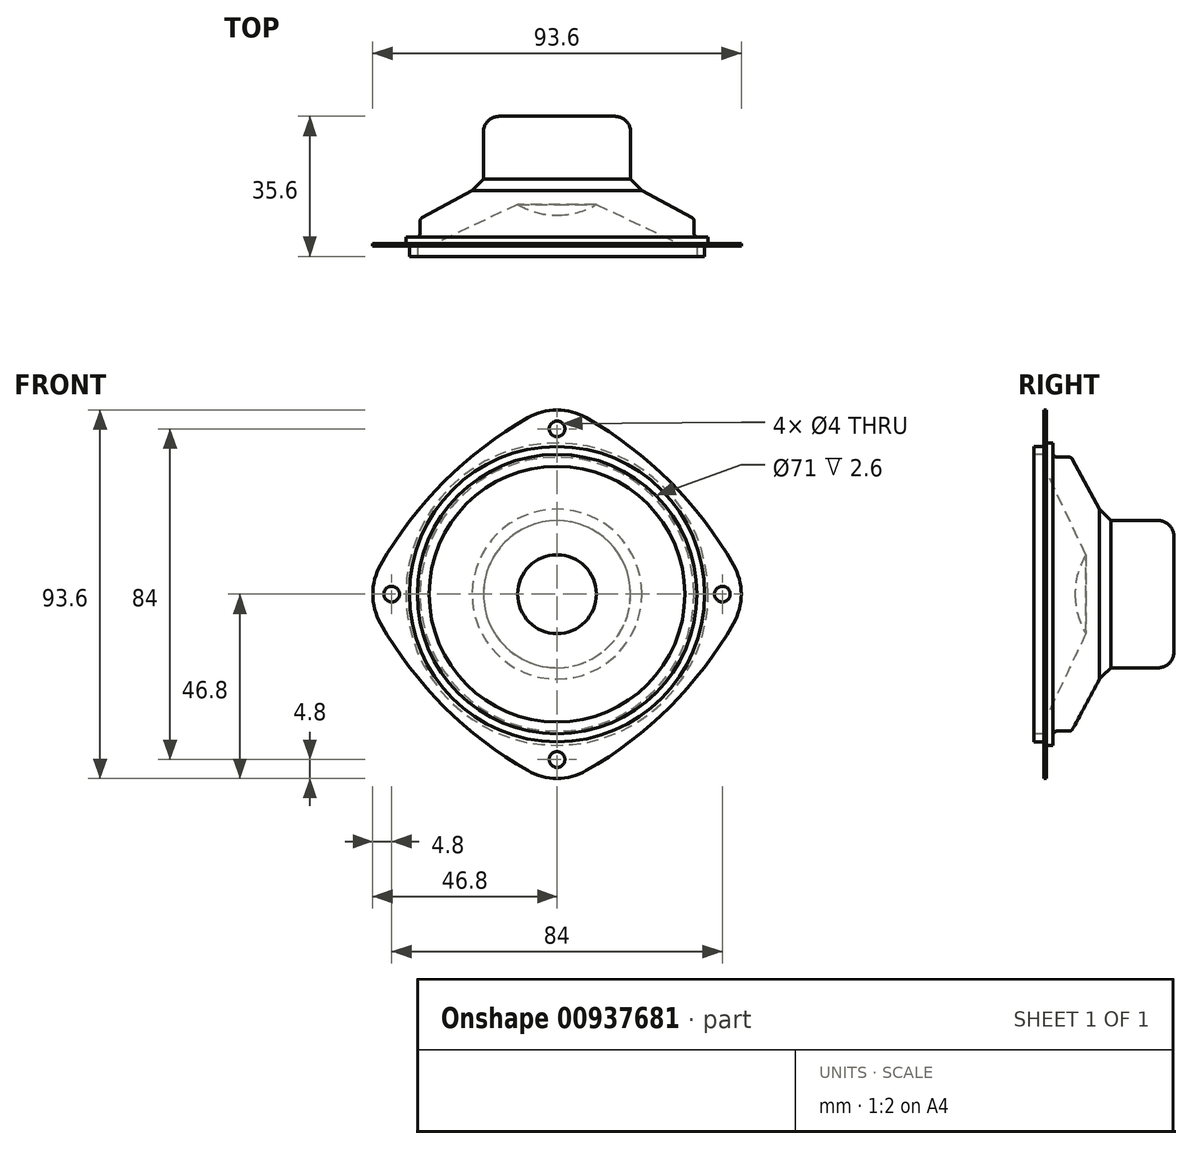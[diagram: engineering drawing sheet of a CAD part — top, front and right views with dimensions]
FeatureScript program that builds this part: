
annotation { "Feature Type Name" : "Feature", "Feature Type Description" : "" }
export const myFeature = defineFeature(function(context is Context, id is Id, definition is map)
    precondition{}
    {
        {
            var Q0;
            Q0=qCreatedBy(makeId("Top.planeOp"),FACE);
            var sketch = newSketch(context, id + "F0", { "sketchPlane" : qUnion([Q0])});
            skLineSegment(sketch, "E0", {"start": v(0, -15.16) * mm, "end": v(0, 70.73) * mm, "construction": true});
            skLineSegment(sketch, "E1", {"start": v(37.5, 0) * mm, "end": v(46.8, 0) * mm});
            skLineSegment(sketch, "E2", {"start": v(37.5, 0) * mm, "end": v(37.5, -2.6) * mm});
            skLineSegment(sketch, "E3", {"start": v(37.5, -2.6) * mm, "end": v(35.5, -2.6) * mm});
            skLineSegment(sketch, "E4", {"start": v(35.5, -2.6) * mm, "end": v(35.5, 0) * mm});
            skLineSegment(sketch, "E5", {"start": v(46.8, 0) * mm, "end": v(46.8, 0.65) * mm});
            skLineSegment(sketch, "E6", {"start": v(46.8, 0.65) * mm, "end": v(38.4, 0.65) * mm});
            skLineSegment(sketch, "E7", {"start": v(38.4, 0.65) * mm, "end": v(38.4, 2.3) * mm});
            skLineSegment(sketch, "E8", {"start": v(38.4, 2.3) * mm, "end": v(34.8, 2.3) * mm});
            skLineSegment(sketch, "E9", {"start": v(34.8, 2.3) * mm, "end": v(34.8, 7) * mm});
            skLineSegment(sketch, "E10", {"start": v(34.8, 7) * mm, "end": v(21.58, 14.1) * mm});
            skLineSegment(sketch, "E11", {"start": v(21.58, 14.1) * mm, "end": v(18.7, 17) * mm});
            skLineSegment(sketch, "E12", {"start": v(18.7, 17) * mm, "end": v(18.7, 33) * mm});
            skLineSegment(sketch, "E13", {"start": v(18.7, 33) * mm, "end": v(0, 33) * mm});
            skLineSegment(sketch, "E14", {"start": v(0, 0) * mm, "end": v(35.5, 0) * mm});
            skLineSegment(sketch, "E15", {"start": v(0, 33) * mm, "end": v(0, 0) * mm});
            skLineSegment(sketch, "E16", {"start": v(32.48, 0) * mm, "end": v(10.02, 10.63) * mm});
            skArc(sketch, "E17", {"start": v(10.02, 10.63) * mm, "mid": v(5.2, 8.58) * mm, "end": v(0, 7.89) * mm});
            skSolve(sketch);
        }
        {
            var Q0;
            Q0=makeQuery(id+"F0.imprint","IMPRINT",FACE,{"disambiguationData":[TD([[makeQuery(id+"F0.imprint","IMPRINT",EDGE,{"derivedFrom":sQuery(id+"F0.wireOp",EDGE,"E1")}),1.0]])]});
            var Q1;
            Q1=sQuery(id+"F0.wireOp",EDGE,"E0");
            revolve(context, id + "F1", {"surfaceOperationType" : NewSurfaceOperationType.NEW, "entities" : qUnion([Q0]), "axis" : qUnion([Q1]), "revolveType" : RevolveType.FULL});
        }
        {
            var Q0;
            Q0=makeQuery(id+"F1.opRevolve","SWEPT_EDGE",EDGE,{"disambiguationData":[OSD([sQuery(id+"F0.wireOp",EDGE,"E12"),sQuery(id+"F0.wireOp",EDGE,"E13")])]});
            fillet(context, id + "F2", {"entities" : qUnion([Q0]), "radius" : 4 * mm, "tangentPropagation" : true, "allowEdgeOverflow" : false});
        }
        {
            var Q0;
            Q0=makeQuery(id+"F1.opRevolve","SWEPT_EDGE",EDGE,{"disambiguationData":[OSD([sQuery(id+"F0.wireOp",EDGE,"E9"),sQuery(id+"F0.wireOp",EDGE,"E10")])]});
            var Q1;
            Q1=makeQuery(id+"F1.opRevolve","SWEPT_EDGE",EDGE,{"disambiguationData":[OSD([sQuery(id+"F0.wireOp",EDGE,"E8"),sQuery(id+"F0.wireOp",EDGE,"E9")])]});
            fillet(context, id + "F3", {"entities" : qUnion([Q0, Q1]), "radius" : 1 * mm, "tangentPropagation" : true, "allowEdgeOverflow" : false});
        }
        {
            var Q0;
            Q0=makeQuery(id+"F1.opRevolve","SWEPT_FACE",FACE,{"disambiguationData":[OSD([sQuery(id+"F0.wireOp",EDGE,"E1")])]});
            var sketch = newSketch(context, id + "F4", { "sketchPlane" : qUnion([Q0])});
            skCircle(sketch, "E18", {"center": v(0, 42) * mm, "radius": 2 * mm});
            skCircle(sketch, "E19.1.0", {"center": v(-42, 0) * mm, "radius": 2 * mm});
            skCircle(sketch, "E19.2.0", {"center": v(0, -42) * mm, "radius": 2 * mm});
            skCircle(sketch, "E19.3.0", {"center": v(42, 0) * mm, "radius": 2 * mm});
            skPoint(sketch, "E19.center", {"position": v(0, 0) * mm});
            skArc(sketch, "E20", {"start": v(7.42, 44.83) * mm, "mid": v(0, 46.8) * mm, "end": v(-7.42, 44.83) * mm});
            skArc(sketch, "E21.1.0", {"start": v(-44.83, 7.42) * mm, "mid": v(-46.8, 0) * mm, "end": v(-44.83, -7.42) * mm});
            skArc(sketch, "E21.2.0", {"start": v(-7.42, -44.83) * mm, "mid": v(0, -46.8) * mm, "end": v(7.42, -44.83) * mm});
            skArc(sketch, "E21.3.0", {"start": v(44.83, -7.42) * mm, "mid": v(46.8, 0) * mm, "end": v(44.83, 7.42) * mm});
            skArc(sketch, "E22", {"start": v(44.83, 7.42) * mm, "mid": v(28.65, 28.65) * mm, "end": v(7.42, 44.83) * mm});
            skArc(sketch, "E23.1.0", {"start": v(7.42, -44.83) * mm, "mid": v(28.65, -28.65) * mm, "end": v(44.83, -7.42) * mm});
            skArc(sketch, "E23.2.0", {"start": v(-44.83, -7.42) * mm, "mid": v(-28.65, -28.65) * mm, "end": v(-7.42, -44.83) * mm});
            skArc(sketch, "E23.3.0", {"start": v(-7.42, 44.83) * mm, "mid": v(-28.65, 28.65) * mm, "end": v(-44.83, 7.42) * mm});
            skLineSegment(sketch, "E23.anchor1", {"start": v(0, 0) * mm, "end": v(-42.06, -42.06) * mm, "construction": true});
            skLineSegment(sketch, "E23.anchor2", {"start": v(0, 0) * mm, "end": v(42.06, -42.06) * mm, "construction": true});
            skCircle(sketch, "E24", {"center": v(0, 0) * mm, "radius": 46.8 * mm});
            skSolve(sketch);
        }
        {
            var Q0;
            {var subQ0=sQuery(id+"F4.wireOp",EDGE,"E23.1.0");Q0=makeQuery(id+"F4.imprint","IMPRINT",FACE,{"disambiguationData":[TD([[makeQuery(id+"F4.imprint","IMPRINT",EDGE,{"derivedFrom":subQ0}),-1.0]])]});}
            var Q1;
            {var subQ0=sQuery(id+"F4.wireOp",EDGE,"E23.2.0");Q1=makeQuery(id+"F4.imprint","IMPRINT",FACE,{"disambiguationData":[TD([[makeQuery(id+"F4.imprint","IMPRINT",EDGE,{"derivedFrom":subQ0}),-1.0]])]});}
            var Q2;
            {var subQ0=sQuery(id+"F4.wireOp",EDGE,"E23.3.0");Q2=makeQuery(id+"F4.imprint","IMPRINT",FACE,{"disambiguationData":[TD([[makeQuery(id+"F4.imprint","IMPRINT",EDGE,{"derivedFrom":subQ0}),-1.0]])]});}
            var Q3;
            {var subQ0=sQuery(id+"F4.wireOp",EDGE,"E22");Q3=makeQuery(id+"F4.imprint","IMPRINT",FACE,{"disambiguationData":[TD([[makeQuery(id+"F4.imprint","IMPRINT",EDGE,{"derivedFrom":subQ0}),-1.0]])]});}
            var Q4;
            Q4=makeQuery(id+"F4.imprint","IMPRINT",FACE,{"disambiguationData":[TD([[makeQuery(id+"F4.imprint","IMPRINT",EDGE,{"derivedFrom":sQuery(id+"F4.wireOp",EDGE,"E19.2.0")}),1.0]])]});
            var Q5;
            Q5=makeQuery(id+"F4.imprint","IMPRINT",FACE,{"disambiguationData":[TD([[makeQuery(id+"F4.imprint","IMPRINT",EDGE,{"derivedFrom":sQuery(id+"F4.wireOp",EDGE,"E18")}),1.0]])]});
            var Q6;
            Q6=makeQuery(id+"F4.imprint","IMPRINT",FACE,{"disambiguationData":[TD([[makeQuery(id+"F4.imprint","IMPRINT",EDGE,{"derivedFrom":sQuery(id+"F4.wireOp",EDGE,"E19.1.0")}),1.0]])]});
            var Q7;
            Q7=makeQuery(id+"F4.imprint","IMPRINT",FACE,{"disambiguationData":[TD([[makeQuery(id+"F4.imprint","IMPRINT",EDGE,{"derivedFrom":sQuery(id+"F4.wireOp",EDGE,"E19.3.0")}),1.0]])]});
            extrude(context, id + "F5", {"entities" : qUnion([Q0, Q1, Q2, Q3, Q4, Q5, Q6, Q7]), "operationType" : NewBodyOperationType.REMOVE, "oppositeDirection" : true, "depth" : 25 * mm, "offsetDistance" : 25 * mm});
        }
    });
